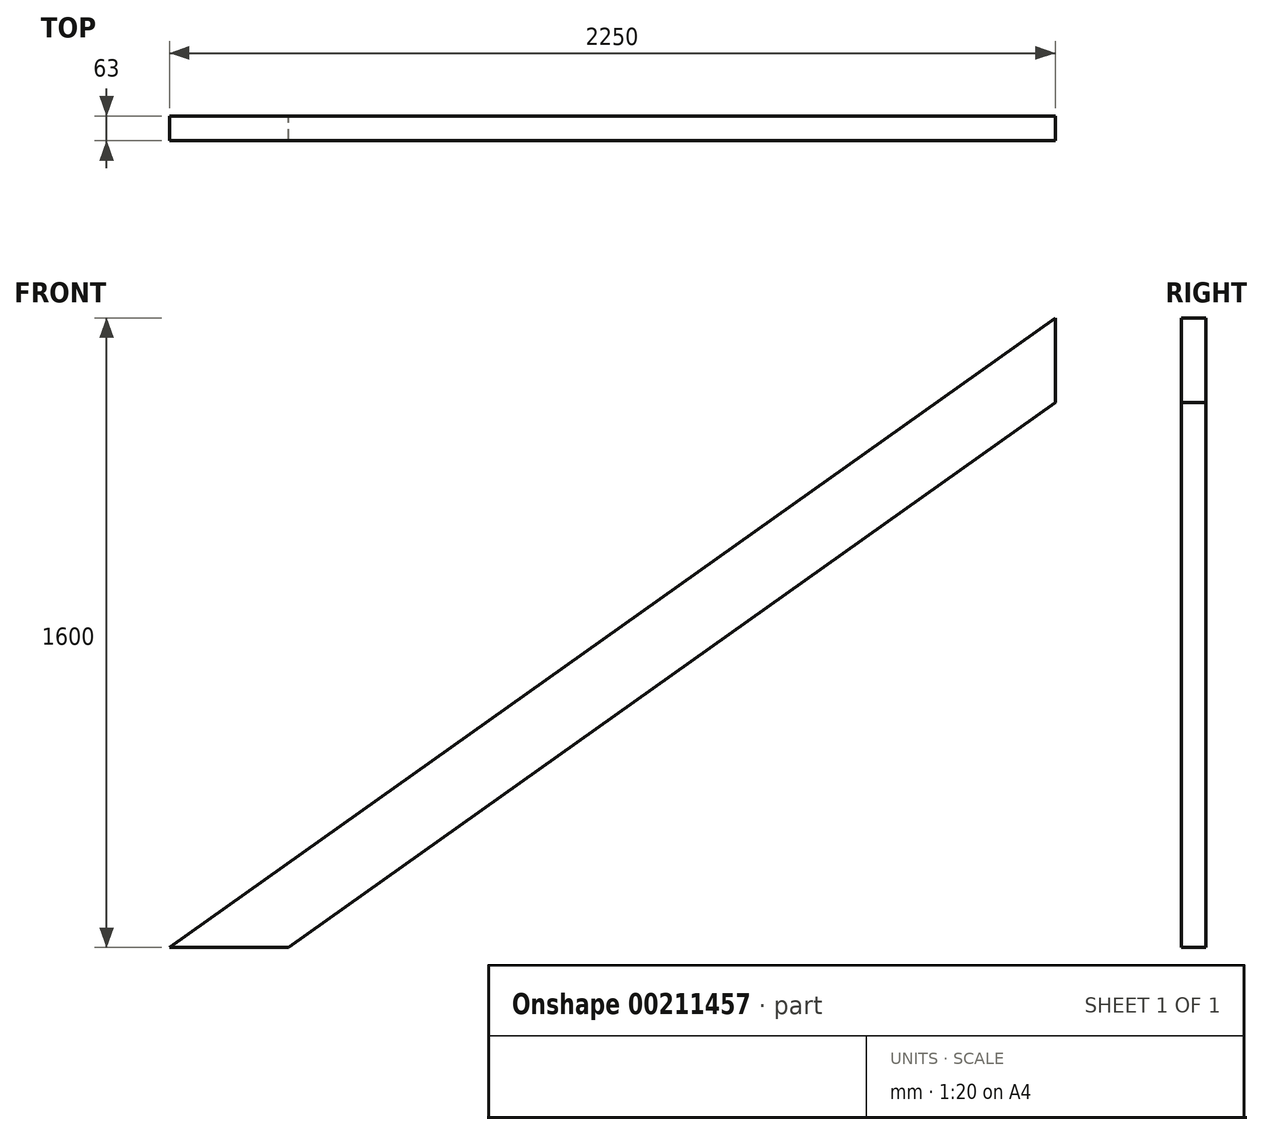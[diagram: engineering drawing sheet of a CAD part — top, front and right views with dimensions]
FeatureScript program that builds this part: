
annotation { "Feature Type Name" : "Feature", "Feature Type Description" : "" }
export const myFeature = defineFeature(function(context is Context, id is Id, definition is map)
    precondition{}
    {
        {
            var Q0;
            Q0=qCreatedBy(makeId("Front.planeOp"),FACE);
            var sketch = newSketch(context, id + "F0", { "sketchPlane" : qUnion([Q0])});
            skLineSegment(sketch, "E0", {"start": v(-644.12, 0) * mm, "end": v(-342.15, 0) * mm});
            skLineSegment(sketch, "E1", {"start": v(-342.15, 0) * mm, "end": v(1605.88, 1385.26) * mm});
            skLineSegment(sketch, "E2", {"start": v(1605.88, 1385.26) * mm, "end": v(1605.88, 1600) * mm});
            skLineSegment(sketch, "E3", {"start": v(1605.88, 1600) * mm, "end": v(-644.12, 0) * mm});
            skSolve(sketch);
        }
        {
            var Q0;
            Q0=qSketchRegion(id+"F0",true);
            extrude(context, id + "F1", {"entities" : qUnion([Q0]), "depth" : 63 * mm});
        }
    });
